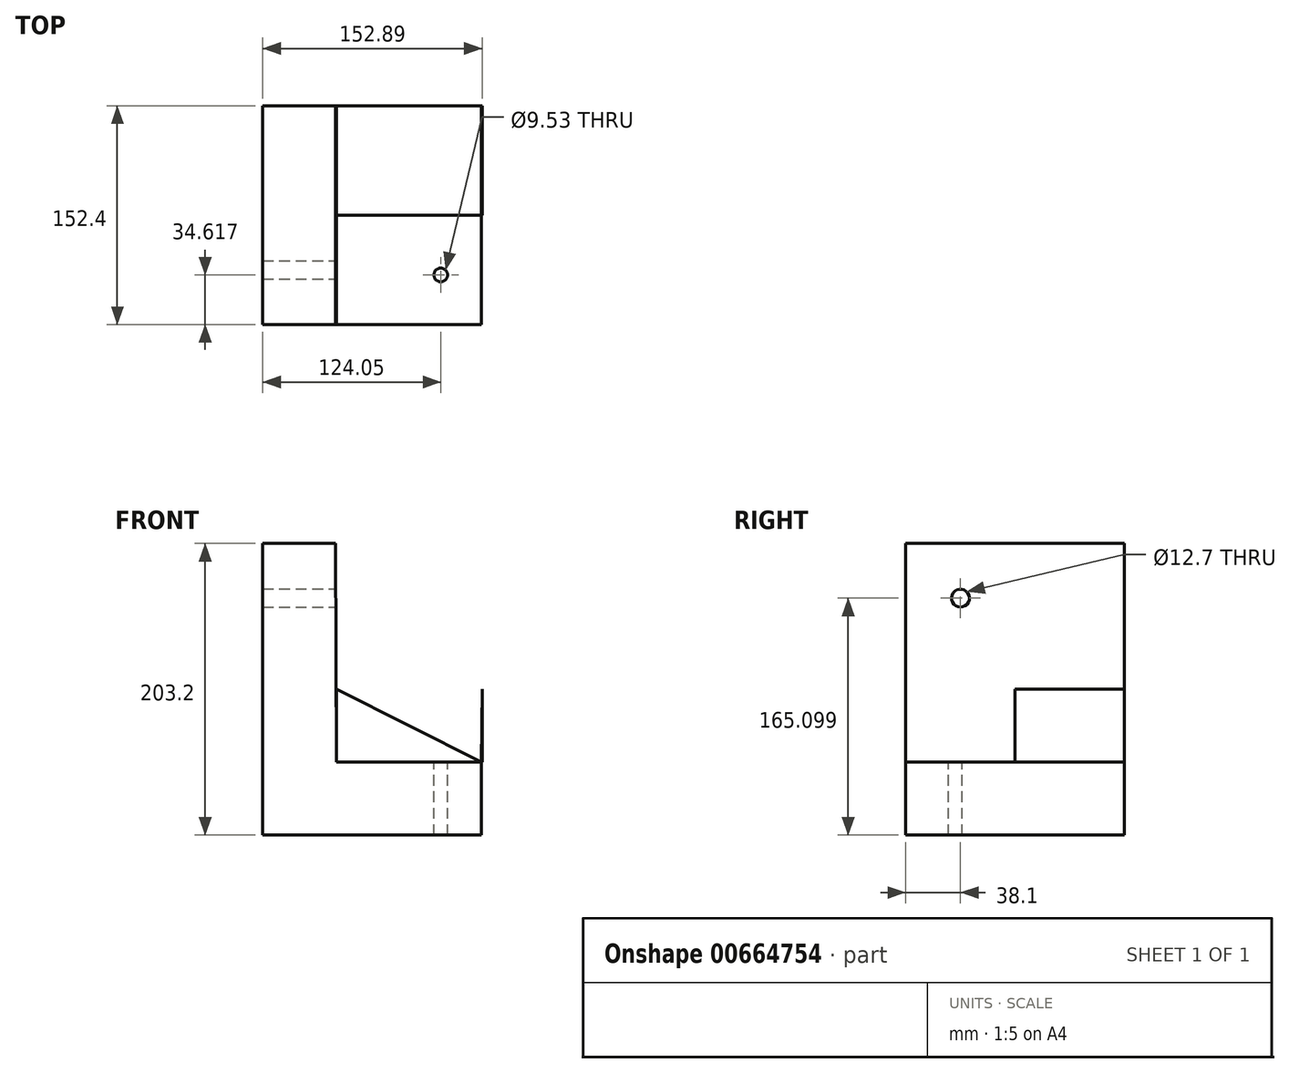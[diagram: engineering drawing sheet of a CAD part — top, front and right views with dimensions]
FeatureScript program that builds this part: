
annotation { "Feature Type Name" : "Feature", "Feature Type Description" : "" }
export const myFeature = defineFeature(function(context is Context, id is Id, definition is map)
    precondition{}
    {
        {
            var Q0;
            Q0=qCreatedBy(makeId("Front.planeOp"),FACE);
            var sketch = newSketch(context, id + "F0", { "sketchPlane" : qUnion([Q0])});
            skLineSegment(sketch, "E0", {"start": v(-42.58, 147.28) * mm, "end": v(8.22, 147.28) * mm});
            skLineSegment(sketch, "E1", {"start": v(8.22, 147.28) * mm, "end": v(-42.58, 147.28) * mm});
            skLineSegment(sketch, "E2", {"start": v(-42.58, 147.28) * mm, "end": v(-42.58, -55.92) * mm});
            skLineSegment(sketch, "E3", {"start": v(-42.58, -55.92) * mm, "end": v(109.82, -55.92) * mm});
            skLineSegment(sketch, "E4", {"start": v(109.82, -55.92) * mm, "end": v(109.82, -5.12) * mm});
            skLineSegment(sketch, "E5", {"start": v(109.82, -5.12) * mm, "end": v(8.71, -5.12) * mm});
            skLineSegment(sketch, "E6", {"start": v(8.71, -5.12) * mm, "end": v(8.22, 147.28) * mm});
            skSolve(sketch);
        }
        {
            var Q0;
            Q0 = qSketchRegion(id + "F0", true);
            extrude(context, id + "F1", {"entities" : qUnion([Q0]), "depth" : 152.4 * mm, "offsetDistance" : 25.4 * mm});
        }
        {
            var Q0;
            Q0=makeQuery(id+"F1.opExtrude","SWEPT_FACE",FACE,{"disambiguationData":[OSD([sQuery(id+"F0.wireOp",EDGE,"E5")])]});
            var sketch = newSketch(context, id + "F2", { "sketchPlane" : qUnion([Q0])});
            skLineSegment(sketch, "E7.bottom", {"start": v(8.71, 0) * mm, "end": v(110.31, 0) * mm});
            skLineSegment(sketch, "E7.top", {"start": v(8.71, -76.2) * mm, "end": v(110.31, -76.2) * mm});
            skLineSegment(sketch, "E7.left", {"start": v(8.71, 0) * mm, "end": v(8.71, -76.2) * mm});
            skLineSegment(sketch, "E7.right", {"start": v(110.31, 0) * mm, "end": v(110.31, -76.2) * mm});
            skSolve(sketch);
        }
        {
            var Q0;
            Q0 = qSketchRegion(id + "F2", true);
            extrude(context, id + "F3", {"entities" : qUnion([Q0]), "operationType" : NewBodyOperationType.ADD, "depth" : 50.8 * mm, "offsetDistance" : 25.4 * mm});
        }
        {
            var Q0;
            Q0=makeQuery(id+"F3.opExtrude","SWEPT_FACE",FACE,{"disambiguationData":[OSD([sQuery(id+"F2.wireOp",EDGE,"E7.top")])]});
            var sketch = newSketch(context, id + "F4", { "sketchPlane" : qUnion([Q0])});
            skLineSegment(sketch, "E8", {"start": v(8.71, 45.68) * mm, "end": v(109.82, -5.12) * mm});
            skLineSegment(sketch, "E9", {"start": v(8.71, 45.68) * mm, "end": v(110.31, 45.68) * mm});
            skLineSegment(sketch, "E10", {"start": v(110.31, 45.68) * mm, "end": v(109.82, -5.12) * mm});
            skSolve(sketch);
        }
        {
            var Q0;
            Q0=makeQuery(id+"F4.imprint","IMPRINT",FACE,{"disambiguationData":[TD([[makeQuery(id+"F4.imprint","IMPRINT",EDGE,{"derivedFrom":sQuery(id+"F4.wireOp",EDGE,"E8")}),1.0]])]});
            extrude(context, id + "F5", {"entities" : qUnion([Q0]), "operationType" : NewBodyOperationType.REMOVE, "oppositeDirection" : true, "depth" : 76.2 * mm, "offsetDistance" : 25.4 * mm});
        }
        {
            var Q0;
            Q0=makeQuery(id+"F1.opExtrude","SWEPT_FACE",FACE,{"disambiguationData":[OSD([sQuery(id+"F0.wireOp",EDGE,"E5")])]});
            var sketch = newSketch(context, id + "F6", { "sketchPlane" : qUnion([Q0])});
            skCircle(sketch, "E11", {"center": v(81.47, -117.78) * mm, "radius": 4.76 * mm});
            skSolve(sketch);
        }
        {
            var Q0;
            Q0 = qSketchRegion(id + "F6", true);
            extrude(context, id + "F7", {"entities" : qUnion([Q0]), "operationType" : NewBodyOperationType.REMOVE, "oppositeDirection" : true, "depth" : 101.6 * mm, "offsetDistance" : 25.4 * mm});
        }
        {
            var Q0;
            Q0=makeQuery(id+"F3.opExtrude","SWEPT_FACE",FACE,{"disambiguationData":[OSD([sQuery(id+"F2.wireOp",EDGE,"E7.right")])]});
            var sketch = newSketch(context, id + "F8", { "sketchPlane" : qUnion([Q0])});
            skPoint(sketch, "E12", {"position": v(-114.3, 109.18) * mm});
            skSolve(sketch);
        }
        {
            var Q0;
            Q0=sQuery(id+"F8.wireOp",VERTEX,"E12");
            var Q1;
            Q1=makeQuery(id+"F5.boolean.opBoolean","SPLIT",BODY,{"disambiguationData":[OD(0.0)],"derivedFrom":makeQuery(id+"F1.opExtrude","SWEPT_BODY",BODY,{"disambiguationData":[OSD([sQuery(id+"F0.wireOp",EDGE,"E1"),sQuery(id+"F0.wireOp",EDGE,"E2"),sQuery(id+"F0.wireOp",EDGE,"E3"),sQuery(id+"F0.wireOp",EDGE,"E4"),sQuery(id+"F0.wireOp",EDGE,"E5"),sQuery(id+"F0.wireOp",EDGE,"E6")])]})});
            hole(context, id + "F9", {"style" : HoleStyle.SIMPLE, "endStyle" : HoleEndStyle.THROUGH, "holeDiameter" : 12.7 * mm, "majorDiameter" : 6.35 * mm, "isTappedThrough" : true, "tappedDepth" : 12.7 * mm, "tapClearance" : 3, "locations" : qUnion([Q0]), "scope" : qUnion([Q1])});
        }
        {
            var Q0;
            Q0=makeQuery(id+"F1.opExtrude","SWEPT_FACE",FACE,{"disambiguationData":[OSD([sQuery(id+"F0.wireOp",EDGE,"E5")])]});
            extrude(context, id + "F10", {"entities" : qUnion([Q0]), "operationType" : NewBodyOperationType.REMOVE, "depth" : 101.6 * mm, "offsetDistance" : 25.4 * mm});
        }
    });
